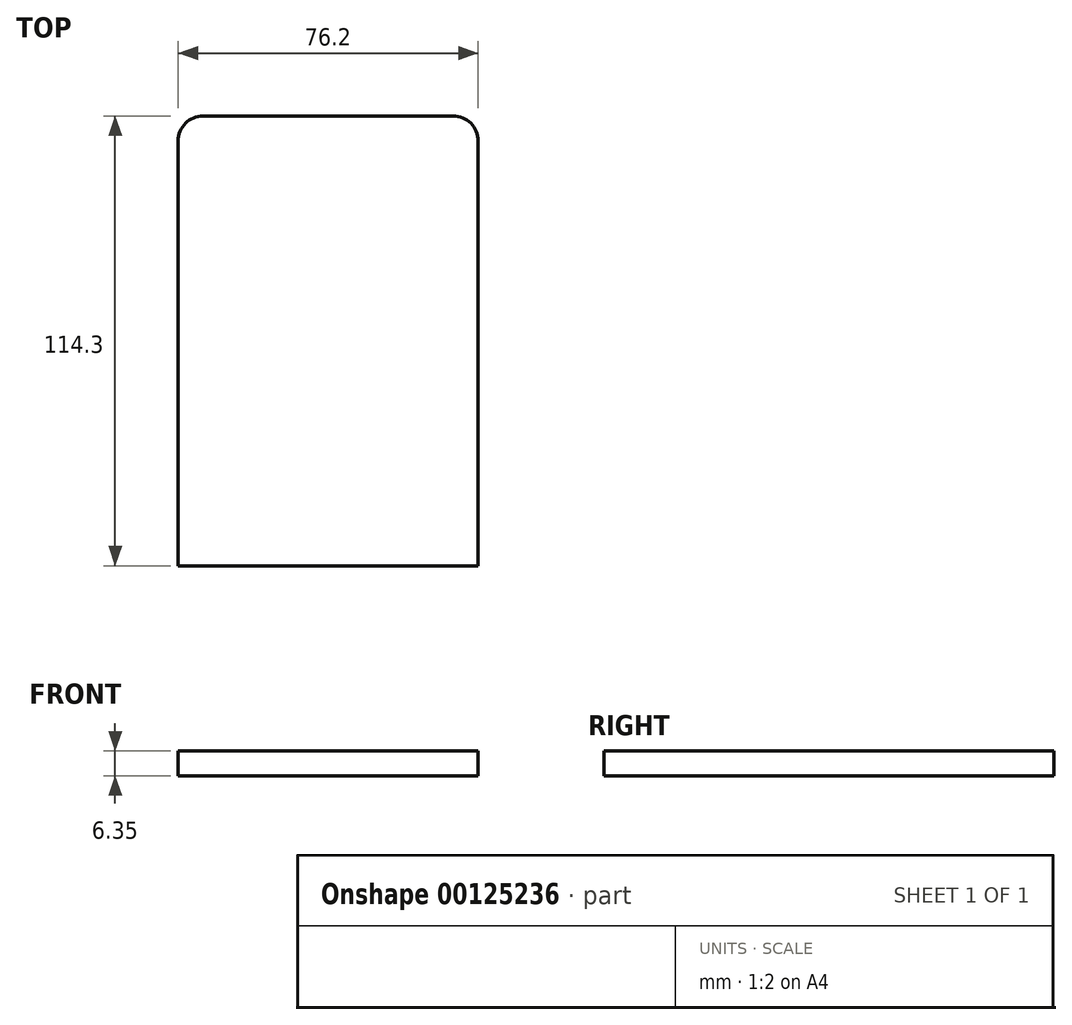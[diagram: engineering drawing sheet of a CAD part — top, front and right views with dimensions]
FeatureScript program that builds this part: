
annotation { "Feature Type Name" : "Feature", "Feature Type Description" : "" }
export const myFeature = defineFeature(function(context is Context, id is Id, definition is map)
    precondition{}
    {
        {
            var Q0;
            Q0=qCreatedBy(makeId("Top.planeOp"),FACE);
            var sketch = newSketch(context, id + "F0", { "sketchPlane" : qUnion([Q0])});
            skLineSegment(sketch, "E0.bottom", {"start": v(-38.82, 81.08) * mm, "end": v(24.68, 81.08) * mm});
            skLineSegment(sketch, "E0.top", {"start": v(-45.17, -33.22) * mm, "end": v(31.03, -33.22) * mm});
            skLineSegment(sketch, "E0.left", {"start": v(-45.17, 74.73) * mm, "end": v(-45.17, -33.22) * mm});
            skLineSegment(sketch, "E0.right", {"start": v(31.03, 74.73) * mm, "end": v(31.03, -33.22) * mm});
            skPoint(sketch, "E1.visualSharp", {"position": v(31.03, 81.08) * mm});
            skArc(sketch, "E1.filletArc", {"start": v(31.03, 74.73) * mm, "mid": v(29.17, 79.22) * mm, "end": v(24.68, 81.08) * mm});
            skPoint(sketch, "E2.visualSharp", {"position": v(-45.17, 81.08) * mm});
            skArc(sketch, "E2.filletArc", {"start": v(-38.82, 81.08) * mm, "mid": v(-43.31, 79.22) * mm, "end": v(-45.17, 74.73) * mm});
            skSolve(sketch);
        }
        {
            var Q0;
            Q0=makeQuery(id+"F0.imprint","IMPRINT",FACE,{"disambiguationData":[TD([[makeQuery(id+"F0.imprint","IMPRINT",EDGE,{"derivedFrom":sQuery(id+"F0.wireOp",EDGE,"E0.bottom")}),-1.0]])]});
            extrude(context, id + "F1", {"entities" : qUnion([Q0]), "depth" : 6.35 * mm});
        }
    });
